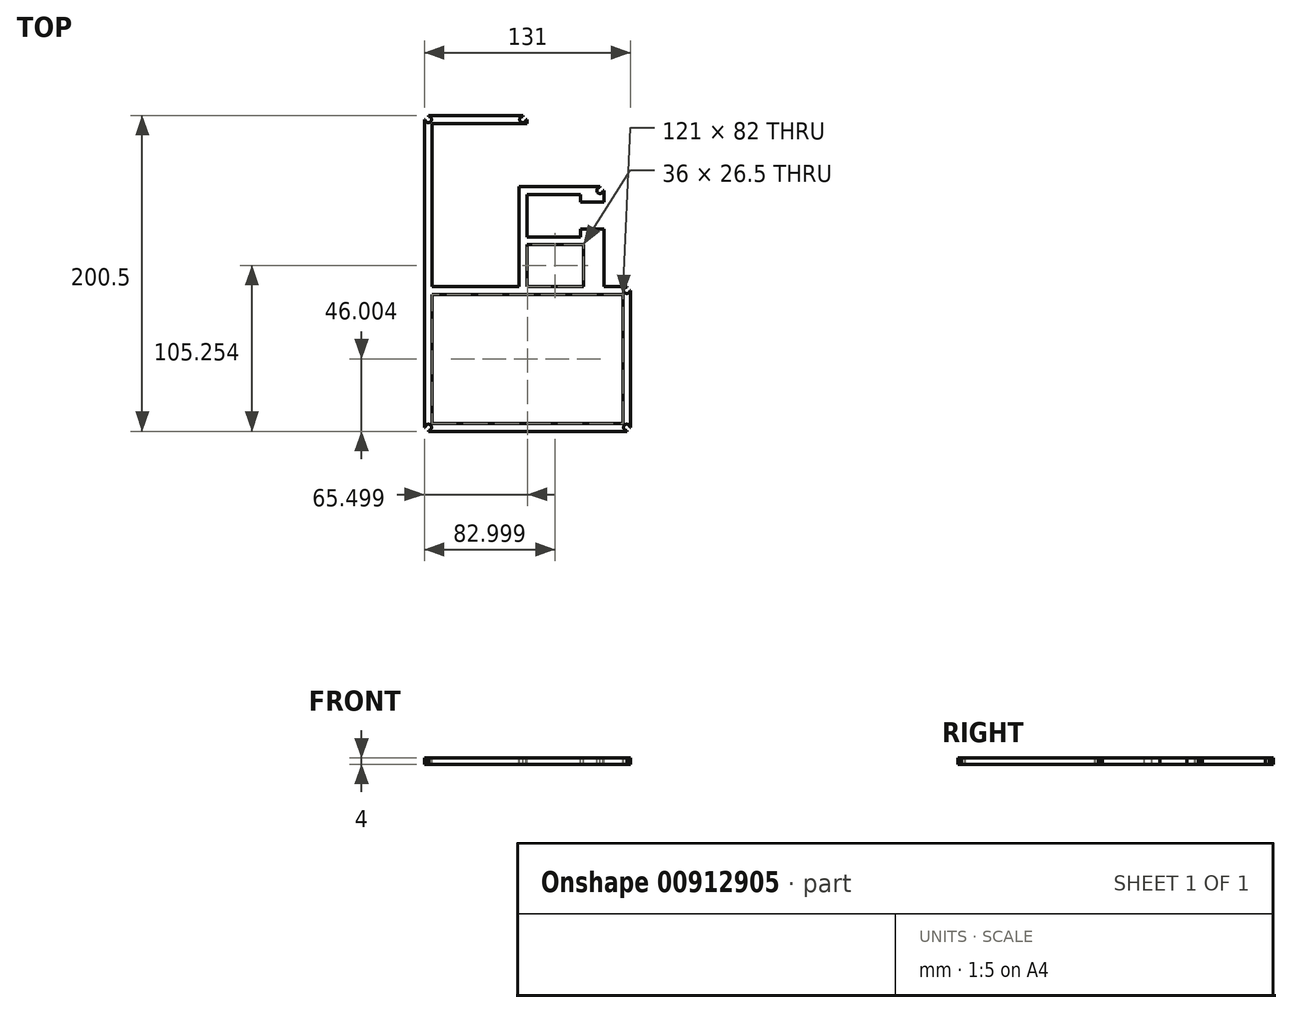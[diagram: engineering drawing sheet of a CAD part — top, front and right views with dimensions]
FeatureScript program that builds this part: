
annotation { "Feature Type Name" : "Feature", "Feature Type Description" : "" }
export const myFeature = defineFeature(function(context is Context, id is Id, definition is map)
    precondition{}
    {
        {
            var Q0;
            Q0=qCreatedBy(makeId("Top.planeOp"),FACE);
            var sketch = newSketch(context, id + "F0", { "sketchPlane" : qUnion([Q0])});
            skLineSegment(sketch, "E0.bottom", {"start": v(-40.7, -58.83) * mm, "end": v(14.3, -58.83) * mm});
            skLineSegment(sketch, "E0.top", {"start": v(-40.7, 44.67) * mm, "end": v(14.3, 44.67) * mm});
            skLineSegment(sketch, "E0.left", {"start": v(-40.7, -58.83) * mm, "end": v(-40.7, 44.67) * mm});
            skLineSegment(sketch, "E0.right", {"start": v(14.3, -58.83) * mm, "end": v(14.3, 44.67) * mm});
            skLineSegment(sketch, "E1.bottom", {"start": v(-45.7, 49.67) * mm, "end": v(85.3, 49.67) * mm});
            skLineSegment(sketch, "E1.top", {"start": v(-45.7, -150.83) * mm, "end": v(85.3, -150.83) * mm});
            skLineSegment(sketch, "E1.left", {"start": v(-45.7, 49.67) * mm, "end": v(-45.7, -150.83) * mm});
            skLineSegment(sketch, "E1.right", {"start": v(85.3, 49.67) * mm, "end": v(85.3, -150.83) * mm});
            skLineSegment(sketch, "E2.bottom", {"start": v(-40.7, -63.83) * mm, "end": v(80.3, -63.83) * mm});
            skLineSegment(sketch, "E2.top", {"start": v(-40.7, -145.83) * mm, "end": v(80.3, -145.83) * mm});
            skLineSegment(sketch, "E2.left", {"start": v(-40.7, -63.83) * mm, "end": v(-40.7, -145.83) * mm});
            skLineSegment(sketch, "E2.right", {"start": v(80.3, -63.83) * mm, "end": v(80.3, -145.83) * mm});
            skLineSegment(sketch, "E3.top", {"start": v(14.3, -63.83) * mm, "end": v(19.3, -63.83) * mm});
            skLineSegment(sketch, "E4.bottom", {"start": v(19.3, -58.83) * mm, "end": v(55.3, -58.83) * mm});
            skLineSegment(sketch, "E4.top", {"start": v(19.3, -32.33) * mm, "end": v(55.3, -32.33) * mm});
            skLineSegment(sketch, "E4.left", {"start": v(19.3, -58.83) * mm, "end": v(19.3, -32.33) * mm});
            skLineSegment(sketch, "E4.right", {"start": v(55.3, -58.83) * mm, "end": v(55.3, -32.33) * mm});
            skLineSegment(sketch, "E5.right", {"start": v(14.3, -32.33) * mm, "end": v(14.3, -27.33) * mm});
            skLineSegment(sketch, "E6.bottom", {"start": v(19.3, -27.33) * mm, "end": v(53.3, -27.33) * mm});
            skLineSegment(sketch, "E6.top", {"start": v(19.3, -0.33) * mm, "end": v(53.3, -0.33) * mm});
            skLineSegment(sketch, "E6.left", {"start": v(19.3, -27.33) * mm, "end": v(19.3, -0.33) * mm});
            skLineSegment(sketch, "E6.right", {"start": v(53.3, -27.33) * mm, "end": v(53.3, -0.33) * mm});
            skLineSegment(sketch, "E7", {"start": v(53.3, -27.33) * mm, "end": v(53.3, -22.33) * mm});
            skLineSegment(sketch, "E8", {"start": v(53.3, -22.33) * mm, "end": v(53.3, -5.33) * mm});
            skLineSegment(sketch, "E9.bottom", {"start": v(53.3, -5.33) * mm, "end": v(53.3, -5.33) * mm});
            skLineSegment(sketch, "E9.top", {"start": v(53.3, -22.33) * mm, "end": v(53.3, -22.33) * mm});
            skLineSegment(sketch, "E9.left", {"start": v(53.3, -5.33) * mm, "end": v(53.3, -22.33) * mm});
            skLineSegment(sketch, "E9.right", {"start": v(53.3, -5.33) * mm, "end": v(53.3, -22.33) * mm});
            skLineSegment(sketch, "E10.bottom", {"start": v(53.3, -22.33) * mm, "end": v(63.3, -22.33) * mm});
            skLineSegment(sketch, "E10.top", {"start": v(53.3, -5.33) * mm, "end": v(63.3, -5.33) * mm});
            skLineSegment(sketch, "E10.right", {"start": v(63.3, -22.33) * mm, "end": v(63.3, -5.33) * mm});
            skLineSegment(sketch, "E11.bottom", {"start": v(14.3, 44.67) * mm, "end": v(19.3, 44.67) * mm});
            skLineSegment(sketch, "E11.top", {"start": v(14.3, 49.67) * mm, "end": v(19.3, 49.67) * mm});
            skLineSegment(sketch, "E11.left", {"start": v(14.3, 44.67) * mm, "end": v(14.3, 49.67) * mm});
            skLineSegment(sketch, "E11.right", {"start": v(19.3, 44.67) * mm, "end": v(19.3, 49.67) * mm});
            skLineSegment(sketch, "E12.bottom", {"start": v(19.3, -0.33) * mm, "end": v(14.3, -0.33) * mm});
            skLineSegment(sketch, "E12.top", {"start": v(19.3, 4.67) * mm, "end": v(14.3, 4.67) * mm});
            skLineSegment(sketch, "E12.left", {"start": v(19.3, -0.33) * mm, "end": v(19.3, 4.67) * mm});
            skLineSegment(sketch, "E12.right", {"start": v(14.3, -0.33) * mm, "end": v(14.3, 4.67) * mm});
            skLineSegment(sketch, "E13.bottom", {"start": v(85.3, 49.67) * mm, "end": v(80.3, 49.67) * mm});
            skLineSegment(sketch, "E13.left", {"start": v(85.3, 49.67) * mm, "end": v(85.3, 44.67) * mm});
            skLineSegment(sketch, "E14.top", {"start": v(19.3, 49.67) * mm, "end": v(85.3, 49.67) * mm});
            skLineSegment(sketch, "E14.left", {"start": v(19.3, 4.67) * mm, "end": v(19.3, 49.67) * mm});
            skLineSegment(sketch, "E14.right", {"start": v(85.3, 4.67) * mm, "end": v(85.3, 49.67) * mm});
            skLineSegment(sketch, "E15.bottom", {"start": v(80.3, -63.83) * mm, "end": v(85.3, -63.83) * mm});
            skLineSegment(sketch, "E15.top", {"start": v(80.3, -58.83) * mm, "end": v(85.3, -58.83) * mm});
            skLineSegment(sketch, "E15.left", {"start": v(80.3, -63.83) * mm, "end": v(80.3, -58.83) * mm});
            skLineSegment(sketch, "E15.right", {"start": v(85.3, -63.83) * mm, "end": v(85.3, -58.83) * mm});
            skLineSegment(sketch, "E16", {"start": v(63.3, -5.33) * mm, "end": v(68.3, -5.33) * mm});
            skLineSegment(sketch, "E17", {"start": v(68.3, -5.33) * mm, "end": v(68.3, -22.33) * mm});
            skLineSegment(sketch, "E18.bottom", {"start": v(85.3, -58.83) * mm, "end": v(68.3, -58.83) * mm});
            skLineSegment(sketch, "E18.left", {"start": v(85.3, -58.83) * mm, "end": v(85.3, 4.67) * mm});
            skLineSegment(sketch, "E18.right", {"start": v(68.3, -58.83) * mm, "end": v(68.3, 4.67) * mm});
            skLineSegment(sketch, "E19", {"start": v(19.3, 4.67) * mm, "end": v(68.3, 4.67) * mm});
            skLineSegment(sketch, "E20.bottom", {"start": v(68.3, 4.67) * mm, "end": v(65.8, 4.67) * mm});
            skLineSegment(sketch, "E20.top", {"start": v(68.3, 2.17) * mm, "end": v(65.8, 2.17) * mm});
            skLineSegment(sketch, "E20.left", {"start": v(68.3, 4.67) * mm, "end": v(68.3, 2.17) * mm});
            skLineSegment(sketch, "E20.right", {"start": v(65.8, 4.67) * mm, "end": v(65.8, 2.17) * mm});
            skLineSegment(sketch, "E21.bottom", {"start": v(19.3, 44.67) * mm, "end": v(16.8, 44.67) * mm});
            skLineSegment(sketch, "E21.top", {"start": v(19.3, 47.17) * mm, "end": v(16.8, 47.17) * mm});
            skLineSegment(sketch, "E21.left", {"start": v(19.3, 44.67) * mm, "end": v(19.3, 47.17) * mm});
            skLineSegment(sketch, "E22.bottom", {"start": v(85.3, -58.83) * mm, "end": v(82.8, -58.83) * mm});
            skLineSegment(sketch, "E22.top", {"start": v(85.3, -61.33) * mm, "end": v(82.8, -61.33) * mm});
            skLineSegment(sketch, "E22.left", {"start": v(85.3, -58.83) * mm, "end": v(85.3, -61.33) * mm});
            skLineSegment(sketch, "E22.right", {"start": v(82.8, -58.83) * mm, "end": v(82.8, -61.33) * mm});
            skLineSegment(sketch, "E23.bottom", {"start": v(85.3, -150.83) * mm, "end": v(82.8, -150.83) * mm});
            skLineSegment(sketch, "E23.top", {"start": v(85.3, -148.33) * mm, "end": v(82.8, -148.33) * mm});
            skLineSegment(sketch, "E23.left", {"start": v(85.3, -150.83) * mm, "end": v(85.3, -148.33) * mm});
            skLineSegment(sketch, "E23.right", {"start": v(82.8, -150.83) * mm, "end": v(82.8, -148.33) * mm});
            skLineSegment(sketch, "E24.bottom", {"start": v(-45.7, -150.83) * mm, "end": v(-43.2, -150.83) * mm});
            skLineSegment(sketch, "E24.top", {"start": v(-45.7, -148.33) * mm, "end": v(-43.2, -148.33) * mm});
            skLineSegment(sketch, "E24.left", {"start": v(-45.7, -150.83) * mm, "end": v(-45.7, -148.33) * mm});
            skLineSegment(sketch, "E24.right", {"start": v(-43.2, -150.83) * mm, "end": v(-43.2, -148.33) * mm});
            skLineSegment(sketch, "E25.bottom", {"start": v(-45.7, 49.67) * mm, "end": v(-43.2, 49.67) * mm});
            skLineSegment(sketch, "E25.top", {"start": v(-45.7, 47.17) * mm, "end": v(-43.2, 47.17) * mm});
            skLineSegment(sketch, "E25.left", {"start": v(-45.7, 49.67) * mm, "end": v(-45.7, 47.17) * mm});
            skLineSegment(sketch, "E25.right", {"start": v(-43.2, 49.67) * mm, "end": v(-43.2, 47.17) * mm});
            skLineSegment(sketch, "E26.bottom", {"start": v(19.3, 49.67) * mm, "end": v(16.8, 49.67) * mm});
            skLineSegment(sketch, "E26.left", {"start": v(19.3, 49.67) * mm, "end": v(19.3, 47.17) * mm});
            skLineSegment(sketch, "E26.right", {"start": v(16.8, 49.67) * mm, "end": v(16.8, 47.17) * mm});
            skCircle(sketch, "E27", {"center": v(16.8, 47.17) * mm, "radius": 2 * mm});
            skCircle(sketch, "E28", {"center": v(65.8, 2.17) * mm, "radius": 2 * mm});
            skCircle(sketch, "E29", {"center": v(82.8, -61.33) * mm, "radius": 2 * mm});
            skCircle(sketch, "E30", {"center": v(82.8, -148.33) * mm, "radius": 2 * mm});
            skCircle(sketch, "E31", {"center": v(-43.2, -148.33) * mm, "radius": 2 * mm});
            skCircle(sketch, "E32", {"center": v(-43.2, 47.17) * mm, "radius": 2 * mm});
            skLineSegment(sketch, "E33.bottom", {"start": v(-40.7, -63.83) * mm, "end": v(-37.3, -63.83) * mm});
            skLineSegment(sketch, "E33.top", {"start": v(-40.7, -67.23) * mm, "end": v(-37.3, -67.23) * mm});
            skLineSegment(sketch, "E33.left", {"start": v(-40.7, -63.83) * mm, "end": v(-40.7, -67.23) * mm});
            skLineSegment(sketch, "E33.right", {"start": v(-37.3, -63.83) * mm, "end": v(-37.3, -67.23) * mm});
            skLineSegment(sketch, "E34.bottom", {"start": v(-40.7, -145.83) * mm, "end": v(-37.3, -145.83) * mm});
            skLineSegment(sketch, "E34.top", {"start": v(-40.7, -142.43) * mm, "end": v(-37.3, -142.43) * mm});
            skLineSegment(sketch, "E34.left", {"start": v(-40.7, -145.83) * mm, "end": v(-40.7, -142.43) * mm});
            skLineSegment(sketch, "E34.right", {"start": v(-37.3, -145.83) * mm, "end": v(-37.3, -142.43) * mm});
            skLineSegment(sketch, "E35.bottom", {"start": v(80.3, -145.83) * mm, "end": v(76.9, -145.83) * mm});
            skLineSegment(sketch, "E35.top", {"start": v(80.3, -142.43) * mm, "end": v(76.9, -142.43) * mm});
            skLineSegment(sketch, "E35.left", {"start": v(80.3, -145.83) * mm, "end": v(80.3, -142.43) * mm});
            skLineSegment(sketch, "E35.right", {"start": v(76.9, -145.83) * mm, "end": v(76.9, -142.43) * mm});
            skLineSegment(sketch, "E36.bottom", {"start": v(80.3, -63.83) * mm, "end": v(76.9, -63.83) * mm});
            skLineSegment(sketch, "E36.top", {"start": v(80.3, -67.23) * mm, "end": v(76.9, -67.23) * mm});
            skLineSegment(sketch, "E36.left", {"start": v(80.3, -63.83) * mm, "end": v(80.3, -67.23) * mm});
            skLineSegment(sketch, "E36.right", {"start": v(76.9, -63.83) * mm, "end": v(76.9, -67.23) * mm});
            skLineSegment(sketch, "E37.bottom", {"start": v(-40.7, -58.83) * mm, "end": v(-37.7, -58.83) * mm});
            skLineSegment(sketch, "E37.top", {"start": v(-40.7, 28.47) * mm, "end": v(-37.7, 28.47) * mm});
            skLineSegment(sketch, "E37.left", {"start": v(-40.7, -58.83) * mm, "end": v(-40.7, 28.47) * mm});
            skLineSegment(sketch, "E37.right", {"start": v(-37.7, -58.83) * mm, "end": v(-37.7, 28.47) * mm});
            skLineSegment(sketch, "E38.bottom", {"start": v(-37.7, -58.83) * mm, "end": v(-40.7, -58.83) * mm});
            skLineSegment(sketch, "E38.top", {"start": v(-37.7, -52.83) * mm, "end": v(-40.7, -52.83) * mm});
            skLineSegment(sketch, "E38.left", {"start": v(-37.7, -58.83) * mm, "end": v(-37.7, -52.83) * mm});
            skLineSegment(sketch, "E38.right", {"start": v(-40.7, -58.83) * mm, "end": v(-40.7, -52.83) * mm});
            skLineSegment(sketch, "E39.bottom", {"start": v(14.3, -58.83) * mm, "end": v(11.3, -58.83) * mm});
            skLineSegment(sketch, "E39.top", {"start": v(14.3, 29.87) * mm, "end": v(11.3, 29.87) * mm});
            skLineSegment(sketch, "E39.left", {"start": v(14.3, -58.83) * mm, "end": v(14.3, 29.87) * mm});
            skLineSegment(sketch, "E39.right", {"start": v(11.3, -58.83) * mm, "end": v(11.3, 29.87) * mm});
            skLineSegment(sketch, "E40.top", {"start": v(14.3, -47.23) * mm, "end": v(11.3, -47.23) * mm});
            skLineSegment(sketch, "E40.left", {"start": v(14.3, -58.83) * mm, "end": v(14.3, -47.23) * mm});
            skLineSegment(sketch, "E40.right", {"start": v(11.3, -58.83) * mm, "end": v(11.3, -47.23) * mm});
            skCircle(sketch, "E41", {"center": v(-37.7, -52.83) * mm, "radius": 2 * mm});
            skCircle(sketch, "E42", {"center": v(-37.7, 28.47) * mm, "radius": 2 * mm});
            skCircle(sketch, "E43", {"center": v(11.3, 29.87) * mm, "radius": 2 * mm});
            skCircle(sketch, "E44", {"center": v(11.3, -47.23) * mm, "radius": 2 * mm});
            skLineSegment(sketch, "E45.bottom", {"start": v(19.3, -0.33) * mm, "end": v(28.55, -0.33) * mm});
            skLineSegment(sketch, "E45.top", {"start": v(19.3, -2.28) * mm, "end": v(28.55, -2.28) * mm});
            skLineSegment(sketch, "E45.left", {"start": v(19.3, -0.33) * mm, "end": v(19.3, -2.28) * mm});
            skLineSegment(sketch, "E45.right", {"start": v(28.55, -0.33) * mm, "end": v(28.55, -2.28) * mm});
            skLineSegment(sketch, "E46.bottom", {"start": v(19.3, -27.33) * mm, "end": v(28.55, -27.33) * mm});
            skLineSegment(sketch, "E46.top", {"start": v(19.3, -25.38) * mm, "end": v(28.55, -25.38) * mm});
            skLineSegment(sketch, "E46.left", {"start": v(19.3, -27.33) * mm, "end": v(19.3, -25.38) * mm});
            skLineSegment(sketch, "E46.right", {"start": v(28.55, -27.33) * mm, "end": v(28.55, -25.38) * mm});
            skLineSegment(sketch, "E47.bottom", {"start": v(53.3, -0.33) * mm, "end": v(51.35, -0.33) * mm});
            skLineSegment(sketch, "E47.top", {"start": v(53.3, -2.28) * mm, "end": v(51.35, -2.28) * mm});
            skLineSegment(sketch, "E47.left", {"start": v(53.3, -0.33) * mm, "end": v(53.3, -2.28) * mm});
            skLineSegment(sketch, "E47.right", {"start": v(51.35, -0.33) * mm, "end": v(51.35, -2.28) * mm});
            skLineSegment(sketch, "E48.bottom", {"start": v(53.3, -27.33) * mm, "end": v(51.35, -27.33) * mm});
            skLineSegment(sketch, "E48.top", {"start": v(53.3, -25.38) * mm, "end": v(51.35, -25.38) * mm});
            skLineSegment(sketch, "E48.left", {"start": v(53.3, -27.33) * mm, "end": v(53.3, -25.38) * mm});
            skLineSegment(sketch, "E48.right", {"start": v(51.35, -27.33) * mm, "end": v(51.35, -25.38) * mm});
            skLineSegment(sketch, "E49.bottom", {"start": v(55.3, -32.33) * mm, "end": v(53.6, -32.33) * mm});
            skLineSegment(sketch, "E49.top", {"start": v(55.3, -34.03) * mm, "end": v(53.6, -34.03) * mm});
            skLineSegment(sketch, "E49.left", {"start": v(55.3, -32.33) * mm, "end": v(55.3, -34.03) * mm});
            skLineSegment(sketch, "E49.right", {"start": v(53.6, -32.33) * mm, "end": v(53.6, -34.03) * mm});
            skLineSegment(sketch, "E50.bottom", {"start": v(55.3, -58.83) * mm, "end": v(53.6, -58.83) * mm});
            skLineSegment(sketch, "E50.top", {"start": v(55.3, -57.13) * mm, "end": v(53.6, -57.13) * mm});
            skLineSegment(sketch, "E50.left", {"start": v(55.3, -58.83) * mm, "end": v(55.3, -57.13) * mm});
            skLineSegment(sketch, "E50.right", {"start": v(53.6, -58.83) * mm, "end": v(53.6, -57.13) * mm});
            skCircle(sketch, "E51", {"center": v(53.6, -34.03) * mm, "radius": 1.2 * mm});
            skCircle(sketch, "E52", {"center": v(53.6, -57.13) * mm, "radius": 1.2 * mm});
            skCircle(sketch, "E53", {"center": v(51.35, -25.38) * mm, "radius": 1.15 * mm});
            skCircle(sketch, "E54", {"center": v(28.55, -25.38) * mm, "radius": 1.15 * mm});
            skCircle(sketch, "E55", {"center": v(28.55, -2.28) * mm, "radius": 1.15 * mm});
            skCircle(sketch, "E56", {"center": v(51.35, -2.28) * mm, "radius": 1.15 * mm});
            skCircle(sketch, "E57", {"center": v(-37.3, -67.23) * mm, "radius": 1.4 * mm});
            skCircle(sketch, "E58", {"center": v(76.9, -67.23) * mm, "radius": 1.4 * mm});
            skCircle(sketch, "E59", {"center": v(-37.3, -142.43) * mm, "radius": 1.4 * mm});
            skCircle(sketch, "E60", {"center": v(76.9, -142.43) * mm, "radius": 1.4 * mm});
            skLineSegment(sketch, "E61", {"start": v(68.3, -22.33) * mm, "end": v(63.3, -22.33) * mm});
            skSolve(sketch);
        }
        {
            var Q0;
            {var subQ1=sQuery(id+"F0.wireOp",EDGE,"E23.bottom");Q0=makeQuery(id+"F0.imprint","IMPRINT",FACE,{"disambiguationData":[TD([[makeQuery(id+"F0.imprint","IMPRINT",EDGE,{"derivedFrom":subQ1}),-1.0]])]});}
            var Q1;
            {var subQ1=sQuery(id+"F0.wireOp",EDGE,"E24.bottom");Q1=makeQuery(id+"F0.imprint","IMPRINT",FACE,{"disambiguationData":[TD([[makeQuery(id+"F0.imprint","IMPRINT",EDGE,{"derivedFrom":subQ1}),1.0]])]});}
            var Q2;
            {var subQ1=sQuery(id+"F0.wireOp",EDGE,"E25.bottom");Q2=makeQuery(id+"F0.imprint","IMPRINT",FACE,{"disambiguationData":[TD([[makeQuery(id+"F0.imprint","IMPRINT",EDGE,{"derivedFrom":subQ1}),-1.0]])]});}
            var Q3;
            {var subQ1=sQuery(id+"F0.wireOp",EDGE,"E22.bottom");Q3=makeQuery(id+"F0.imprint","IMPRINT",FACE,{"disambiguationData":[TD([[makeQuery(id+"F0.imprint","IMPRINT",EDGE,{"derivedFrom":subQ1}),1.0]])]});}
            var Q4;
            {var subQ1=sQuery(id+"F0.wireOp",EDGE,"E26.bottom");Q4=makeQuery(id+"F0.imprint","IMPRINT",FACE,{"disambiguationData":[TD([[makeQuery(id+"F0.imprint","IMPRINT",EDGE,{"derivedFrom":subQ1}),1.0]])]});}
            var Q5;
            Q5=makeQuery(id+"F0.imprint","IMPRINT",FACE,{"disambiguationData":[TD([[makeQuery(id+"F0.imprint","IMPRINT",EDGE,{"derivedFrom":sQuery(id+"F0.wireOp",EDGE,"E15.bottom")}),1.0]])]});
            var Q6;
            Q6=makeQuery(id+"F0.imprint","IMPRINT",FACE,{"disambiguationData":[TD([[makeQuery(id+"F0.imprint","IMPRINT",EDGE,{"derivedFrom":sQuery(id+"F0.wireOp",EDGE,"E11.bottom")}),1.0]])]});
            var Q7;
            Q7=makeQuery(id+"F0.imprint","IMPRINT",FACE,{"disambiguationData":[TD([[makeQuery(id+"F0.imprint","IMPRINT",EDGE,{"derivedFrom":sQuery(id+"F0.wireOp",EDGE,"E0.bottom")}),-1.0]])]});
            var Q8;
            {var subQ0=sQuery(id+"F0.wireOp",EDGE,"E12.bottom");Q8=makeQuery(id+"F0.imprint","IMPRINT",FACE,{"disambiguationData":[TD([[makeQuery(id+"F0.imprint","IMPRINT",EDGE,{"derivedFrom":subQ0}),-1.0]])]});}
            var Q9;
            {var subQ1=sQuery(id+"F0.wireOp",EDGE,"E0.right");Q9=makeQuery(id+"F0.imprint","IMPRINT",FACE,{"disambiguationData":[TD([[makeQuery(id+"F0.imprint","IMPRINT",EDGE,{"derivedFrom":subQ1}),-1.0]])]});}
            var Q10;
            Q10=makeQuery(id+"F0.imprint","IMPRINT",FACE,{"disambiguationData":[TD([[makeQuery(id+"F0.imprint","IMPRINT",EDGE,{"derivedFrom":sQuery(id+"F0.wireOp",EDGE,"E6.top")}),1.0]])]});
            var Q11;
            {var subQ1=sQuery(id+"F0.wireOp",EDGE,"E20.bottom");Q11=makeQuery(id+"F0.imprint","IMPRINT",FACE,{"disambiguationData":[TD([[makeQuery(id+"F0.imprint","IMPRINT",EDGE,{"derivedFrom":subQ1}),1.0]])]});}
            extrude(context, id + "F1", {"entities" : qUnion([Q0, Q1, Q2, Q3, Q4, Q5, Q6, Q7, Q8, Q9, Q10, Q11]), "oppositeDirection" : true, "depth" : 4 * mm, "offsetDistance" : 25 * mm});
        }
    });
